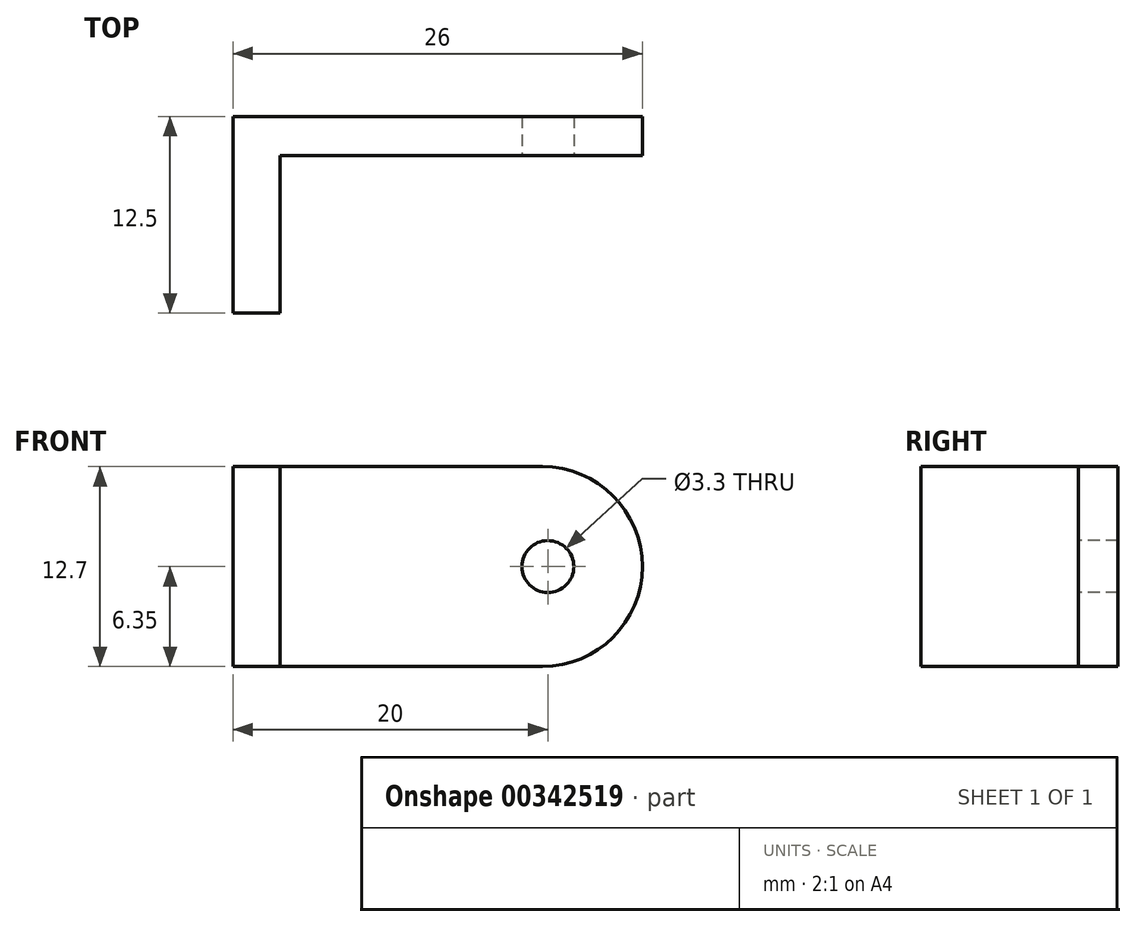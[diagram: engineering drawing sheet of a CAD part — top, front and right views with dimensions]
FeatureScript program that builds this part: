
annotation { "Feature Type Name" : "Feature", "Feature Type Description" : "" }
export const myFeature = defineFeature(function(context is Context, id is Id, definition is map)
    precondition{}
    {
        {
            var Q0;
            Q0=qCreatedBy(makeId("Top.planeOp"),FACE);
            var sketch = newSketch(context, id + "F0", { "sketchPlane" : qUnion([Q0])});
            skLineSegment(sketch, "E0", {"start": v(3, -12.5) * mm, "end": v(3, -2.5) * mm});
            skLineSegment(sketch, "E1", {"start": v(3, -2.5) * mm, "end": v(26, -2.5) * mm});
            skLineSegment(sketch, "E2", {"start": v(26, -2.5) * mm, "end": v(26, 0) * mm});
            skLineSegment(sketch, "E3", {"start": v(26, 0) * mm, "end": v(0, 0) * mm});
            skLineSegment(sketch, "E4", {"start": v(0, 0) * mm, "end": v(0, -12.5) * mm});
            skLineSegment(sketch, "E5", {"start": v(0, -12.5) * mm, "end": v(3, -12.5) * mm});
            skSolve(sketch);
        }
        {
            var Q0;
            Q0=makeQuery(id+"F0.imprint","IMPRINT",FACE,{"disambiguationData":[TD([[makeQuery(id+"F0.imprint","IMPRINT",EDGE,{"derivedFrom":sQuery(id+"F0.wireOp",EDGE,"E0")}),1.0]])]});
            extrude(context, id + "F1", {"entities" : qUnion([Q0]), "depth" : 12.7 * mm, "offsetDistance" : 25.4 * mm});
        }
        {
            var Q0;
            Q0=makeQuery(id+"F1.opExtrude","SWEPT_FACE",FACE,{"disambiguationData":[OSD([sQuery(id+"F0.wireOp",EDGE,"E1")])]});
            var sketch = newSketch(context, id + "F2", { "sketchPlane" : qUnion([Q0])});
            skPoint(sketch, "E6", {"position": v(20, 6.35) * mm});
            skCircle(sketch, "E7", {"center": v(20, 6.35) * mm, "radius": 1.65 * mm});
            skSolve(sketch);
        }
        {
            var Q0;
            Q0=makeQuery(id+"F2.imprint","IMPRINT",FACE,{"disambiguationData":[TD([[makeQuery(id+"F2.imprint","IMPRINT",EDGE,{"derivedFrom":sQuery(id+"F2.wireOp",EDGE,"E7")}),1.0]])]});
            extrude(context, id + "F3", {"entities" : qUnion([Q0]), "operationType" : NewBodyOperationType.REMOVE, "oppositeDirection" : true, "depth" : 3.17 * mm, "offsetDistance" : 25.4 * mm});
        }
        {
            var Q0;
            Q0=makeQuery(id+"F1.opExtrude","CAP_EDGE",EDGE,{"disambiguationData":[OSD([sQuery(id+"F0.wireOp",EDGE,"E2")])],"isStart":false});
            var Q1;
            Q1=makeQuery(id+"F1.opExtrude","CAP_EDGE",EDGE,{"disambiguationData":[OSD([sQuery(id+"F0.wireOp",EDGE,"E2")])],"isStart":true});
            fillet(context, id + "F4", {"entities" : qUnion([Q0, Q1]), "radius" : 6.35 * mm, "tangentPropagation" : true, "allowEdgeOverflow" : false});
        }
    });
